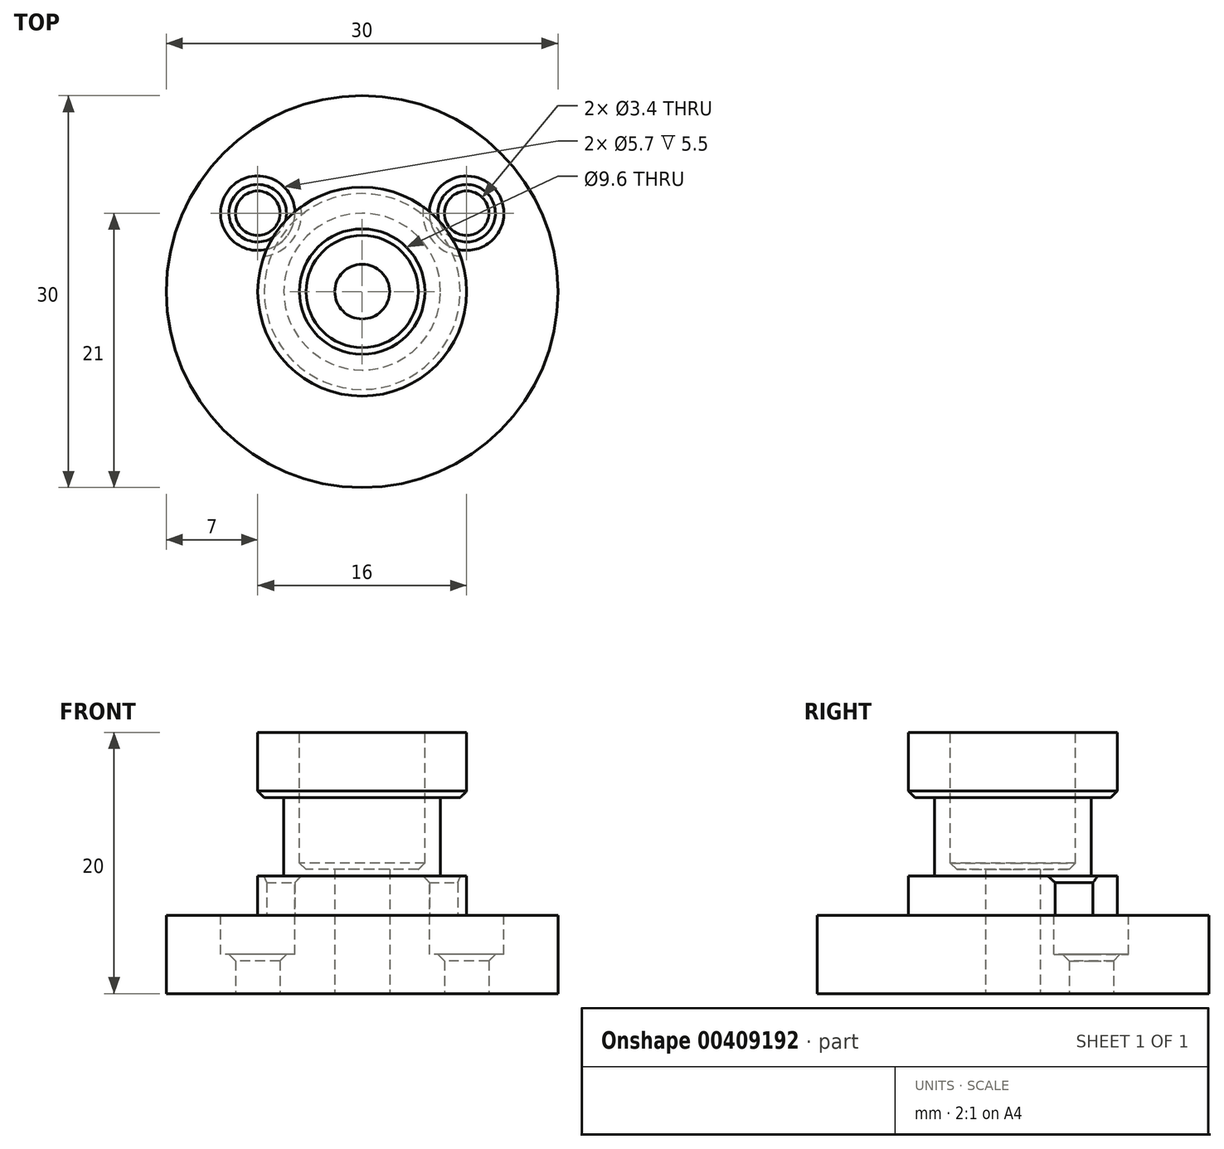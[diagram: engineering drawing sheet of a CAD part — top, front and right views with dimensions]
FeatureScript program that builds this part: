
annotation { "Feature Type Name" : "Feature", "Feature Type Description" : "" }
export const myFeature = defineFeature(function(context is Context, id is Id, definition is map)
    precondition{}
    {
        {
            var Q0;
            Q0=qCreatedBy(makeId("Top.planeOp"),FACE);
            var sketch = newSketch(context, id + "F0", { "sketchPlane" : qUnion([Q0])});
            skCircle(sketch, "E0", {"center": v(0, 0) * mm, "radius": 10 * mm, "construction": true});
            skCircle(sketch, "E1", {"center": v(0, 0) * mm, "radius": 15 * mm});
            skLineSegment(sketch, "E2", {"start": v(-8, 6) * mm, "end": v(8, 6) * mm, "construction": true});
            skCircle(sketch, "E3", {"center": v(-8, 6) * mm, "radius": 1.7 * mm});
            skCircle(sketch, "E4", {"center": v(8, 6) * mm, "radius": 1.7 * mm});
            skCircle(sketch, "E5", {"center": v(0, 0) * mm, "radius": 2.1 * mm});
            skSolve(sketch);
        }
        {
            var Q0;
            Q0=makeQuery(id+"F0.imprint","IMPRINT",FACE,{"disambiguationData":[TD([[makeQuery(id+"F0.imprint","IMPRINT",EDGE,{"derivedFrom":sQuery(id+"F0.wireOp",EDGE,"E1")}),1.0]])]});
            extrude(context, id + "F1", {"entities" : qUnion([Q0]), "depth" : 6 * mm});
        }
        {
            var Q0;
            Q0=makeQuery(id+"F1.opExtrude","CAP_FACE",FACE,{"disambiguationData":[OSD([sQuery(id+"F0.wireOp",EDGE,"E1"),sQuery(id+"F0.wireOp",EDGE,"E3"),sQuery(id+"F0.wireOp",EDGE,"E4"),sQuery(id+"F0.wireOp",EDGE,"E5")])],"isStart":false});
            var sketch = newSketch(context, id + "F2", { "sketchPlane" : qUnion([Q0])});
            skCircle(sketch, "E6", {"center": v(-8, 6) * mm, "radius": 2.85 * mm});
            skCircle(sketch, "E7", {"center": v(8, 6) * mm, "radius": 2.85 * mm});
            skSolve(sketch);
        }
        {
            var Q0;
            Q0 = qSketchRegion(id + "F2", true);
            extrude(context, id + "F3", {"entities" : qUnion([Q0]), "operationType" : NewBodyOperationType.REMOVE, "oppositeDirection" : true, "depth" : 3 * mm});
        }
        {
            var Q0;
            Q0=makeQuery(id+"F1.opExtrude","CAP_FACE",FACE,{"disambiguationData":[OSD([sQuery(id+"F0.wireOp",EDGE,"E1"),sQuery(id+"F0.wireOp",EDGE,"E3"),sQuery(id+"F0.wireOp",EDGE,"E4"),sQuery(id+"F0.wireOp",EDGE,"E5")])],"isStart":false});
            var sketch = newSketch(context, id + "F4", { "sketchPlane" : qUnion([Q0])});
            skCircle(sketch, "E8", {"center": v(0, 0) * mm, "radius": 8 * mm});
            skSolve(sketch);
        }
        {
            var Q0;
            Q0=makeQuery(id+"F4.imprint","IMPRINT",FACE,{"disambiguationData":[TD([[makeQuery(id+"F4.imprint","IMPRINT",EDGE,{"derivedFrom":makeQuery(id+"F1.opExtrude","CAP_EDGE",EDGE,{"disambiguationData":[OSD([sQuery(id+"F0.wireOp",EDGE,"E5")])],"isStart":false})}),-1.0]])]});
            extrude(context, id + "F5", {"entities" : qUnion([Q0]), "operationType" : NewBodyOperationType.ADD, "depth" : 3 * mm});
        }
        {
            var Q0;
            Q0=makeQuery(id+"F5.opExtrude","CAP_FACE",FACE,{"disambiguationData":[OSD([sQuery(id+"F0.wireOp",EDGE,"E5"),sQuery(id+"F2.wireOp",EDGE,"E6"),sQuery(id+"F2.wireOp",EDGE,"E7"),sQuery(id+"F4.wireOp",EDGE,"E8")])],"isStart":false});
            var sketch = newSketch(context, id + "F6", { "sketchPlane" : qUnion([Q0])});
            skCircle(sketch, "E9", {"center": v(0, 0) * mm, "radius": 6 * mm});
            skSolve(sketch);
        }
        {
            var Q0;
            Q0=makeQuery(id+"F6.imprint","IMPRINT",FACE,{"disambiguationData":[TD([[makeQuery(id+"F6.imprint","IMPRINT",EDGE,{"derivedFrom":sQuery(id+"F6.wireOp",EDGE,"E9")}),1.0]])]});
            extrude(context, id + "F7", {"entities" : qUnion([Q0]), "operationType" : NewBodyOperationType.ADD, "depth" : 6 * mm});
        }
        {
            var Q0;
            Q0=makeQuery(id+"F7.opExtrude","CAP_FACE",FACE,{"disambiguationData":[OSD([sQuery(id+"F0.wireOp",EDGE,"E5"),sQuery(id+"F6.wireOp",EDGE,"E9")])],"isStart":false});
            var sketch = newSketch(context, id + "F8", { "sketchPlane" : qUnion([Q0])});
            skCircle(sketch, "E10", {"center": v(0, 0) * mm, "radius": 8 * mm});
            skSolve(sketch);
        }
        {
            var Q0;
            Q0=makeQuery(id+"F8.imprint","IMPRINT",FACE,{"disambiguationData":[TD([[makeQuery(id+"F8.imprint","IMPRINT",EDGE,{"derivedFrom":makeQuery(id+"F7.opExtrude","CAP_EDGE",EDGE,{"disambiguationData":[OSD([sQuery(id+"F6.wireOp",EDGE,"E9")])],"isStart":false})}),1.0]])]});
            var Q1;
            Q1=makeQuery(id+"F8.imprint","IMPRINT",FACE,{"disambiguationData":[TD([[makeQuery(id+"F8.imprint","IMPRINT",EDGE,{"derivedFrom":sQuery(id+"F8.wireOp",EDGE,"E10")}),1.0]])]});
            extrude(context, id + "F9", {"entities" : qUnion([Q0, Q1]), "operationType" : NewBodyOperationType.ADD, "depth" : 5 * mm});
        }
        {
            var Q0;
            Q0=makeQuery(id+"F9.opExtrude","CAP_FACE",FACE,{"disambiguationData":[OSD([sQuery(id+"F0.wireOp",EDGE,"E5"),sQuery(id+"F8.wireOp",EDGE,"E10")])],"isStart":false});
            var sketch = newSketch(context, id + "F10", { "sketchPlane" : qUnion([Q0])});
            skCircle(sketch, "E11", {"center": v(0, 0) * mm, "radius": 4.8 * mm});
            skSolve(sketch);
        }
        {
            var Q0;
            Q0=makeQuery(id+"F10.imprint","IMPRINT",FACE,{"disambiguationData":[TD([[makeQuery(id+"F10.imprint","IMPRINT",EDGE,{"derivedFrom":sQuery(id+"F10.wireOp",EDGE,"E11")}),1.0]])]});
            extrude(context, id + "F11", {"entities" : qUnion([Q0]), "operationType" : NewBodyOperationType.REMOVE, "oppositeDirection" : true, "depth" : 10.5 * mm});
        }
        {
            var Q0;
            Q0=makeQuery(id+"F11.boolean.opBoolean","COPY",EDGE,{"derivedFrom":makeQuery(id+"F11.opExtrude","CAP_EDGE",EDGE,{"disambiguationData":[OSD([sQuery(id+"F10.wireOp",EDGE,"E11")])],"isStart":true})});
            var Q1;
            Q1=makeQuery(id+"F11.boolean.opBoolean","COPY",EDGE,{"derivedFrom":makeQuery(id+"F11.opExtrude","CAP_EDGE",EDGE,{"disambiguationData":[OSD([sQuery(id+"F0.wireOp",EDGE,"E5")])],"isStart":false})});
            var Q2;
            Q2=makeQuery(id+"F11.boolean.opBoolean","COPY",EDGE,{"derivedFrom":makeQuery(id+"F11.opExtrude","CAP_EDGE",EDGE,{"disambiguationData":[OSD([sQuery(id+"F10.wireOp",EDGE,"E11")])],"isStart":false})});
            var Q3;
            Q3=makeQuery(id+"F3.boolean.opBoolean","INTERSECT",EDGE,{"derivedFrom":[makeQuery(id+"F1.opExtrude","SWEPT_FACE",FACE,{"disambiguationData":[OSD([sQuery(id+"F0.wireOp",EDGE,"E3")])]}),makeQuery(id+"F3.opExtrude","CAP_FACE",FACE,{"disambiguationData":[OSD([sQuery(id+"F2.wireOp",EDGE,"E6")])],"isStart":false})]});
            var Q4;
            Q4=makeQuery(id+"F3.boolean.opBoolean","COPY",EDGE,{"derivedFrom":makeQuery(id+"F3.opExtrude","CAP_EDGE",EDGE,{"disambiguationData":[OSD([sQuery(id+"F2.wireOp",EDGE,"E6")])],"isStart":true})});
            var Q5;
            Q5=makeQuery(id+"F3.boolean.opBoolean","INTERSECT",EDGE,{"derivedFrom":[makeQuery(id+"F1.opExtrude","SWEPT_FACE",FACE,{"disambiguationData":[OSD([sQuery(id+"F0.wireOp",EDGE,"E4")])]}),makeQuery(id+"F3.opExtrude","CAP_FACE",FACE,{"disambiguationData":[OSD([sQuery(id+"F2.wireOp",EDGE,"E7")])],"isStart":false})]});
            var Q6;
            Q6=makeQuery(id+"F3.boolean.opBoolean","COPY",EDGE,{"derivedFrom":makeQuery(id+"F3.opExtrude","CAP_EDGE",EDGE,{"disambiguationData":[OSD([sQuery(id+"F2.wireOp",EDGE,"E7")])],"isStart":true})});
            var Q7;
            Q7=makeQuery(id+"F5.opExtrude","CAP_EDGE",EDGE,{"disambiguationData":[OSD([sQuery(id+"F2.wireOp",EDGE,"E7")])],"isStart":false});
            var Q8;
            Q8=makeQuery(id+"F5.opExtrude","CAP_EDGE",EDGE,{"disambiguationData":[OSD([sQuery(id+"F2.wireOp",EDGE,"E6")])],"isStart":false});
            var Q9;
            Q9=makeQuery(id+"F9.opExtrude","CAP_EDGE",EDGE,{"disambiguationData":[OSD([sQuery(id+"F8.wireOp",EDGE,"E10")])],"isStart":true});
            var Q10;
            {var subQ0=sQuery(id+"F4.wireOp",EDGE,"E8");Q10=makeQuery(id+"F5.opExtrude","CAP_EDGE",EDGE,{"disambiguationData":[OSD([subQ0]),TDD([makeQuery(id+"F4.imprint","IMPRINT",EDGE,{"disambiguationData":[TD([[makeQuery(id+"F4.imprint","INTERSECT",VERTEX,{"disambiguationData":[OD(1.0)],"derivedFrom":[makeQuery(id+"F3.boolean.opBoolean","COPY",EDGE,{"derivedFrom":makeQuery(id+"F3.opExtrude","CAP_EDGE",EDGE,{"disambiguationData":[OSD([sQuery(id+"F2.wireOp",EDGE,"E7")])],"isStart":true})}),subQ0]}),1.0]])],"derivedFrom":subQ0})])],"isStart":false});}
            var Q11;
            {var subQ0=sQuery(id+"F4.wireOp",EDGE,"E8");Q11=makeQuery(id+"F5.opExtrude","CAP_EDGE",EDGE,{"disambiguationData":[OSD([subQ0]),TDD([makeQuery(id+"F4.imprint","IMPRINT",EDGE,{"disambiguationData":[TD([[makeQuery(id+"F4.imprint","INTERSECT",VERTEX,{"disambiguationData":[OD(0.0)],"derivedFrom":[makeQuery(id+"F3.boolean.opBoolean","COPY",EDGE,{"derivedFrom":makeQuery(id+"F3.opExtrude","CAP_EDGE",EDGE,{"disambiguationData":[OSD([sQuery(id+"F2.wireOp",EDGE,"E7")])],"isStart":true})}),subQ0]}),-1.0]])],"derivedFrom":subQ0})])],"isStart":false});}
            chamfer(context, id + "F12", {"entities" : qUnion([Q0, Q1, Q2, Q3, Q4, Q5, Q6, Q7, Q8, Q9, Q10, Q11]), "width" : 0.5 * mm, "tangentPropagation" : true});
        }
    });
